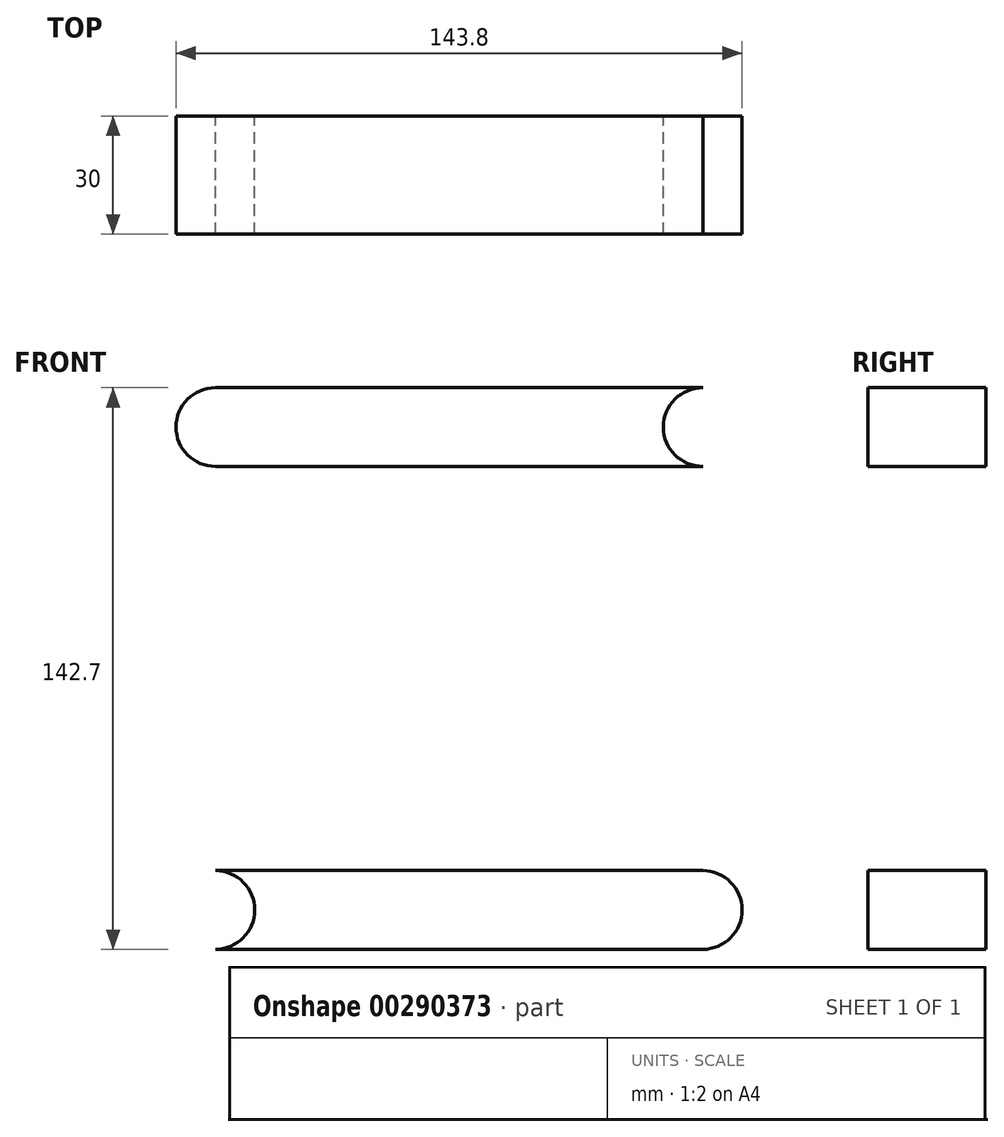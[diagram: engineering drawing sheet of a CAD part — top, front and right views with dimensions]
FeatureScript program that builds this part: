
annotation { "Feature Type Name" : "Feature", "Feature Type Description" : "" }
export const myFeature = defineFeature(function(context is Context, id is Id, definition is map)
    precondition{}
    {
        {
            var Q0;
            Q0=qCreatedBy(makeId("Front.planeOp"),FACE);
            var sketch = newSketch(context, id + "F0", { "sketchPlane" : qUnion([Q0])});
            skCircle(sketch, "E0", {"center": v(-61.9, 61.35) * mm, "radius": 10 * mm});
            skLineSegment(sketch, "E1", {"start": v(-61.9, 71.35) * mm, "end": v(0, 71.35) * mm});
            skLineSegment(sketch, "E2", {"start": v(-61.9, 51.35) * mm, "end": v(0, 51.35) * mm});
            skLineSegment(sketch, "E3", {"start": v(0, 71.35) * mm, "end": v(0, 51.35) * mm});
            skLineSegment(sketch, "E4", {"start": v(-69.55, 0) * mm, "end": v(62.52, 0) * mm, "construction": true});
            skLineSegment(sketch, "E5", {"start": v(0, 41.56) * mm, "end": v(0, -30.16) * mm, "construction": true});
            skCircle(sketch, "E6.MirrorC", {"center": v(-61.9, -61.35) * mm, "radius": 10 * mm});
            skLineSegment(sketch, "E7.MirrorCS", {"start": v(-61.9, -71.35) * mm, "end": v(0, -71.35) * mm});
            skLineSegment(sketch, "E8.MirrorCS", {"start": v(-61.9, -51.35) * mm, "end": v(0, -51.35) * mm});
            skCircle(sketch, "E9.MirrorC", {"center": v(61.9, 61.35) * mm, "radius": 10 * mm});
            skLineSegment(sketch, "E10.MirrorCS", {"start": v(61.9, 71.35) * mm, "end": v(0, 71.35) * mm});
            skLineSegment(sketch, "E11.MirrorCS", {"start": v(61.9, 51.35) * mm, "end": v(0, 51.35) * mm});
            skLineSegment(sketch, "E12.MirrorCS", {"start": v(61.9, -51.35) * mm, "end": v(0, -51.35) * mm});
            skLineSegment(sketch, "E13.MirrorCS", {"start": v(61.9, -71.35) * mm, "end": v(0, -71.35) * mm});
            skCircle(sketch, "E14.MirrorC", {"center": v(61.9, -61.35) * mm, "radius": 10 * mm});
            skSolve(sketch);
        }
        {
            var Q0;
            {var subQ0=sQuery(id+"F0.wireOp",EDGE,"E1");Q0=makeQuery(id+"F0.imprint","IMPRINT",FACE,{"disambiguationData":[TD([[makeQuery(id+"F0.imprint","IMPRINT",EDGE,{"derivedFrom":subQ0}),-1.0]])]});}
            var Q1;
            Q1=makeQuery(id+"F0.imprint","IMPRINT",FACE,{"disambiguationData":[TD([[makeQuery(id+"F0.imprint","IMPRINT",EDGE,{"derivedFrom":sQuery(id+"F0.wireOp",EDGE,"E3")}),1.0]])]});
            var Q2;
            {var subQ0=sQuery(id+"F0.wireOp",EDGE,"E0");var subQ1=makeQuery(id+"F0.imprint","INTERSECT",VERTEX,{"derivedFrom":[subQ0,sQuery(id+"F0.wireOp",EDGE,"E1")]});Q2=makeQuery(id+"F0.imprint","IMPRINT",FACE,{"disambiguationData":[TD([[makeQuery(id+"F0.imprint","IMPRINT",EDGE,{"disambiguationData":[TD([[subQ1,-1.0]])],"derivedFrom":subQ0}),1.0]])]});}
            var Q3;
            {var subQ0=sQuery(id+"F0.wireOp",EDGE,"E9.MirrorC");var subQ1=makeQuery(id+"F0.imprint","INTERSECT",VERTEX,{"derivedFrom":[subQ0,sQuery(id+"F0.wireOp",EDGE,"E10.MirrorCS")]});Q3=makeQuery(id+"F0.imprint","IMPRINT",FACE,{"disambiguationData":[TD([[makeQuery(id+"F0.imprint","IMPRINT",EDGE,{"disambiguationData":[TD([[subQ1,-1.0]])],"derivedFrom":subQ0}),-1.0]])]});}
            var Q4;
            {var subQ0=sQuery(id+"F0.wireOp",EDGE,"E14.MirrorC");var subQ1=makeQuery(id+"F0.imprint","INTERSECT",VERTEX,{"derivedFrom":[sQuery(id+"F0.wireOp",EDGE,"E12.MirrorCS"),subQ0]});Q4=makeQuery(id+"F0.imprint","IMPRINT",FACE,{"disambiguationData":[TD([[makeQuery(id+"F0.imprint","IMPRINT",EDGE,{"disambiguationData":[TD([[subQ1,1.0]])],"derivedFrom":subQ0}),1.0]])]});}
            var Q5;
            {var subQ0=sQuery(id+"F0.wireOp",EDGE,"E6.MirrorC");var subQ1=makeQuery(id+"F0.imprint","INTERSECT",VERTEX,{"derivedFrom":[subQ0,sQuery(id+"F0.wireOp",EDGE,"E7.MirrorCS")]});Q5=makeQuery(id+"F0.imprint","IMPRINT",FACE,{"disambiguationData":[TD([[makeQuery(id+"F0.imprint","IMPRINT",EDGE,{"disambiguationData":[TD([[subQ1,-1.0]])],"derivedFrom":subQ0}),-1.0]])]});}
            var Q6;
            {var subQ2=sQuery(id+"F0.wireOp",EDGE,"E7.MirrorCS");Q6=makeQuery(id+"F0.imprint","IMPRINT",FACE,{"disambiguationData":[TD([[makeQuery(id+"F0.imprint","IMPRINT",EDGE,{"derivedFrom":subQ2}),1.0]])]});}
            extrude(context, id + "F1", {"entities" : qUnion([Q0, Q1, Q2, Q3, Q4, Q5, Q6]), "depth" : 30 * mm});
        }
    });
